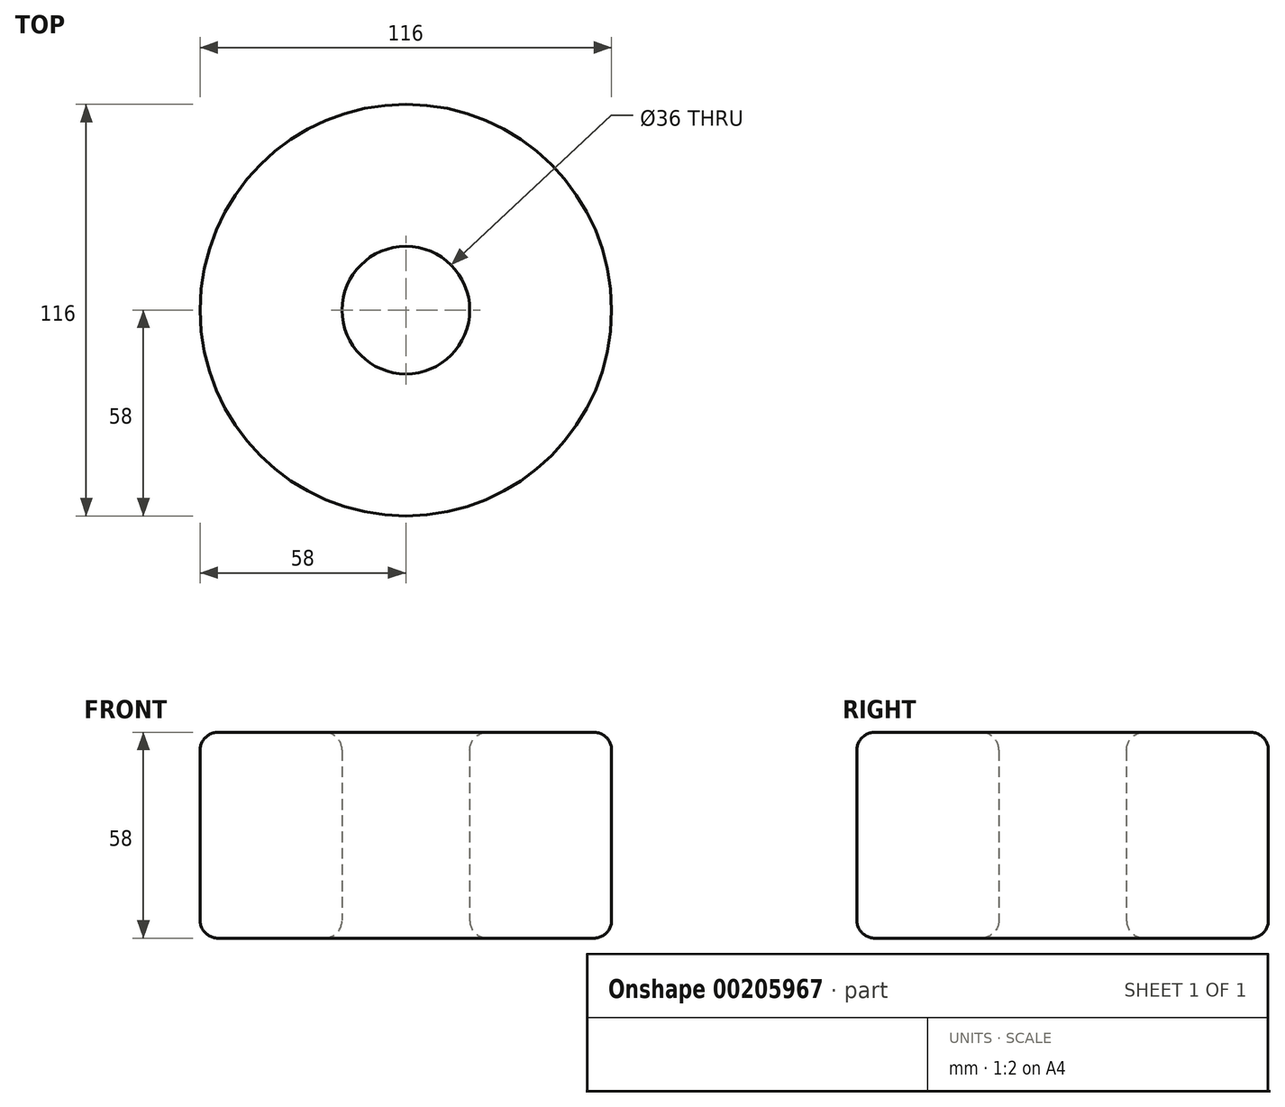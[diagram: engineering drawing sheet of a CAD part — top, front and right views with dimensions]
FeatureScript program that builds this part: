
annotation { "Feature Type Name" : "Feature", "Feature Type Description" : "" }
export const myFeature = defineFeature(function(context is Context, id is Id, definition is map)
    precondition{}
    {
        {
            var Q0;
            Q0=qCreatedBy(makeId("Front.planeOp"),FACE);
            var sketch = newSketch(context, id + "F0", { "sketchPlane" : qUnion([Q0])});
            skLineSegment(sketch, "E0.bottom", {"start": v(-53, 0) * mm, "end": v(-23, 0) * mm});
            skLineSegment(sketch, "E0.top", {"start": v(-53, 58) * mm, "end": v(-23, 58) * mm});
            skLineSegment(sketch, "E0.left", {"start": v(-58, 5) * mm, "end": v(-58, 53) * mm});
            skLineSegment(sketch, "E0.right", {"start": v(-18, 5) * mm, "end": v(-18, 53) * mm});
            skPoint(sketch, "E1.visualSharp", {"position": v(-58, 58) * mm});
            skArc(sketch, "E1.filletArc", {"start": v(-53, 58) * mm, "mid": v(-56.54, 56.54) * mm, "end": v(-58, 53) * mm});
            skPoint(sketch, "E2.visualSharp", {"position": v(-18, 58) * mm});
            skArc(sketch, "E2.filletArc", {"start": v(-18, 53) * mm, "mid": v(-19.46, 56.54) * mm, "end": v(-23, 58) * mm});
            skPoint(sketch, "E3.visualSharp", {"position": v(-18, 0) * mm});
            skArc(sketch, "E3.filletArc", {"start": v(-23, 0) * mm, "mid": v(-19.46, 1.46) * mm, "end": v(-18, 5) * mm});
            skPoint(sketch, "E4.visualSharp", {"position": v(-58, 0) * mm});
            skArc(sketch, "E4.filletArc", {"start": v(-58, 5) * mm, "mid": v(-56.54, 1.46) * mm, "end": v(-53, 0) * mm});
            skLineSegment(sketch, "E5", {"start": v(0, 0) * mm, "end": v(0, 55.18) * mm, "construction": true});
            skSolve(sketch);
        }
        {
            var Q0;
            Q0 = qSketchRegion(id + "F0", true);
            var Q1;
            Q1=sQuery(id+"F0.wireOp",EDGE,"E5");
            revolve(context, id + "F1", {"entities" : qUnion([Q0]), "axis" : qUnion([Q1]), "revolveType" : RevolveType.FULL});
        }
    });
